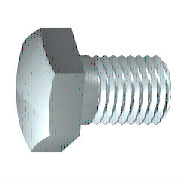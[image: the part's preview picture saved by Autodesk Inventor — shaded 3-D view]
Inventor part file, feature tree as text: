
AUTODESK INVENTOR PART (.ipt)
format: ipt  version: 2023.2 (Build 272271030, 271C)  size: 193,536 bytes
history: native  units: mm (DEFAULTED — no unit token found)
features: sketch x3, extrude x1, chamfer x1, plane x1
ambient origin geometry x7: Origin, YZ Plane, XZ Plane, X Axis, Y Axis, Z Axis, Center Point
bodies: Solid1 (feature_tree), Body (feature_tree)
feature tree (6):
  extrude  "Head"  Depth=30.5mm
  chamfer  "Chamfer1"  Distance=5.8mm
  plane  "Work Plane1"
  sketch  "Sketch1"  dims[d0=35.0mm d1=30.5mm]
  sketch  "Sketch2"  dims[d2=10.0mm]
  sketch  "Sketch4"  dims[d12=90.0deg d3=5.8mm d4=0.0mm d5=30.0deg d21=90.0deg d6=0.920175mm d7=0.920275mm d8=0.0mm d9=0.6001mm d10=14.63mm d11=16.0mm d13=0.920275mm d14=10.0mm d15=30.5mm d16=0.0mm d19=16.0mm d55=45.0deg d57=0.0mm d58=0.0mm]
